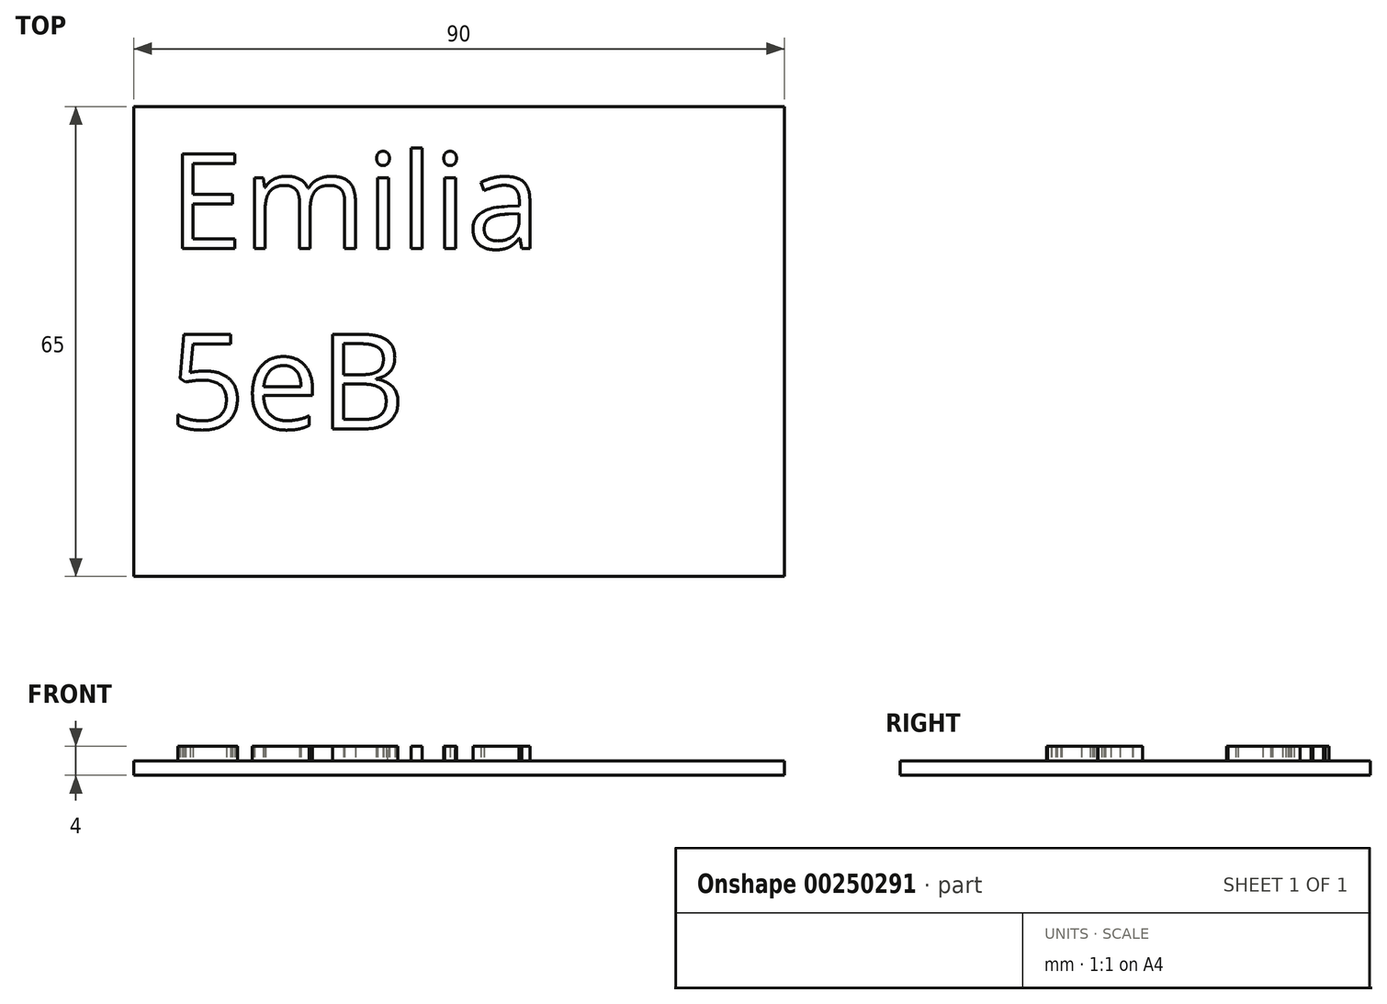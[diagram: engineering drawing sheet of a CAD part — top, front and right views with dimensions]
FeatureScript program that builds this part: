
annotation { "Feature Type Name" : "Feature", "Feature Type Description" : "" }
export const myFeature = defineFeature(function(context is Context, id is Id, definition is map)
    precondition{}
    {
        {
            var Q0;
            Q0=qCreatedBy(makeId("Top.planeOp"),FACE);
            var sketch = newSketch(context, id + "F0", { "sketchPlane" : qUnion([Q0])});
            skLineSegment(sketch, "E0.bottom", {"start": v(0, 0) * mm, "end": v(90, 0) * mm});
            skLineSegment(sketch, "E0.top", {"start": v(0, -65) * mm, "end": v(90, -65) * mm});
            skLineSegment(sketch, "E0.left", {"start": v(0, 0) * mm, "end": v(0, -65) * mm});
            skLineSegment(sketch, "E0.right", {"start": v(90, 0) * mm, "end": v(90, -65) * mm});
            skSolve(sketch);
        }
        {
            var Q0;
            Q0=makeQuery(id+"F0.imprint","IMPRINT",FACE,{"disambiguationData":[TD([[makeQuery(id+"F0.imprint","IMPRINT",EDGE,{"derivedFrom":sQuery(id+"F0.wireOp",EDGE,"E0.bottom")}),-1.0]])]});
            extrude(context, id + "F1", {"entities" : qUnion([Q0]), "depth" : 2 * mm});
        }
        {
            var Q0;
            Q0=makeQuery(id+"F1.opExtrude","CAP_FACE",FACE,{"disambiguationData":[OSD([sQuery(id+"F0.wireOp",EDGE,"E0.bottom"),sQuery(id+"F0.wireOp",EDGE,"E0.top"),sQuery(id+"F0.wireOp",EDGE,"E0.left"),sQuery(id+"F0.wireOp",EDGE,"E0.right")])],"isStart":false});
            var sketch = newSketch(context, id + "F2", { "sketchPlane" : qUnion([Q0])});
            skText(sketch, "E1", { "text": "Emilia\n5eB\n", "fontName": "OpenSans-Regular.ttf"});
            const initialGuessF2  = {"E1": [0.00492, -0.01965, 1, 0, 0.0132]};
            skSetInitialGuess(sketch, initialGuessF2);
            skSolve(sketch);
        }
        {
            var Q0;
            Q0 = qSketchRegion(id + "F2", true);
            extrude(context, id + "F3", {"entities" : qUnion([Q0]), "operationType" : NewBodyOperationType.ADD, "depth" : 2 * mm});
        }
    });
